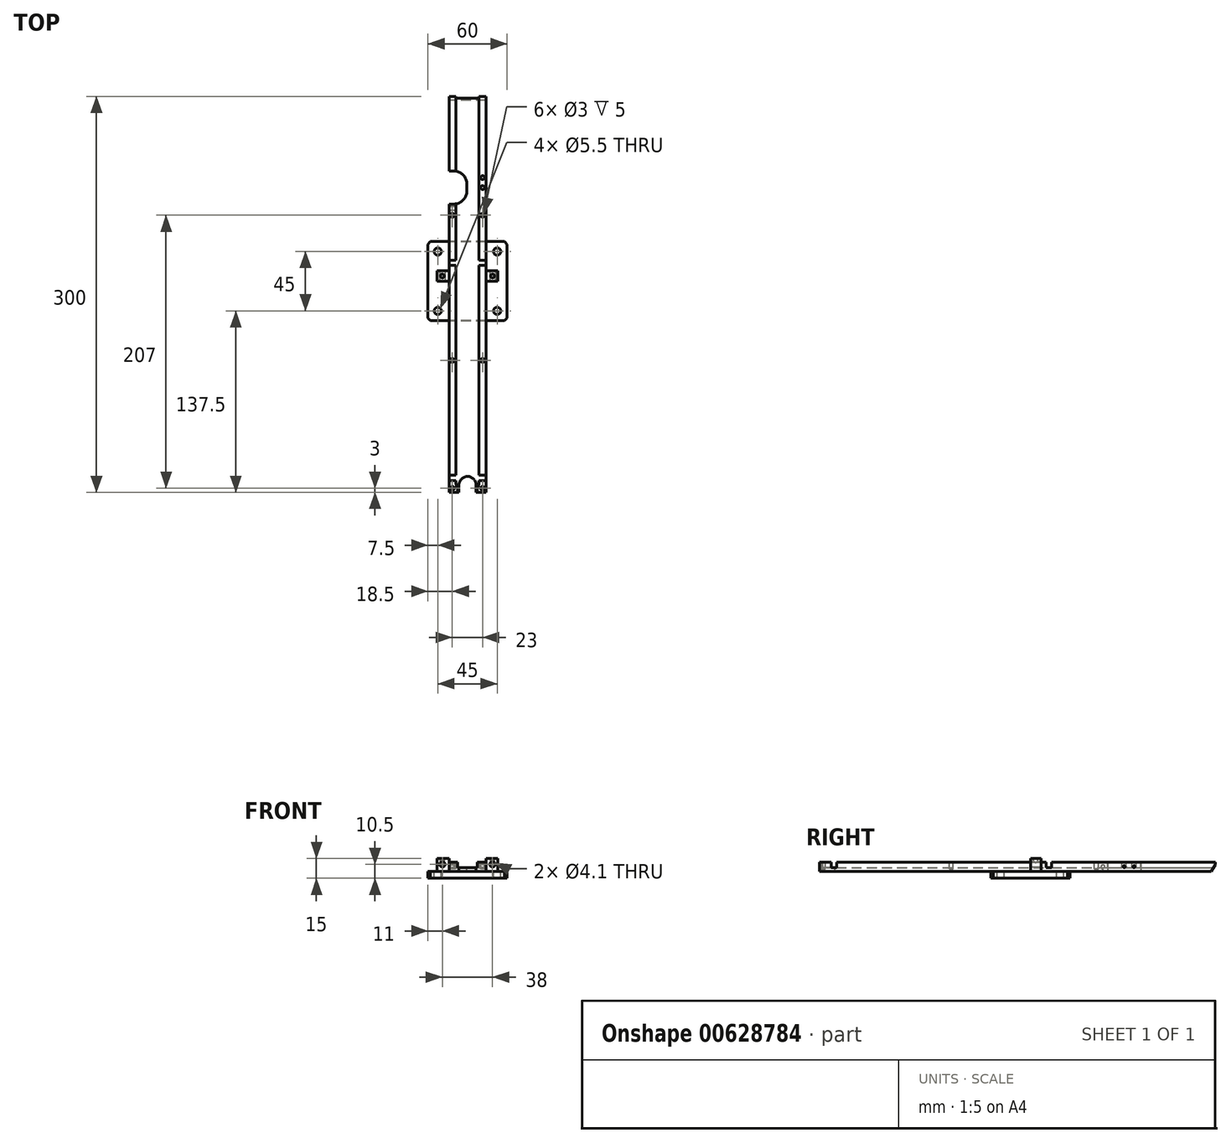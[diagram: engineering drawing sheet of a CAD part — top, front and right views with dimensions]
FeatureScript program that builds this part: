
annotation { "Feature Type Name" : "Feature", "Feature Type Description" : "" }
export const myFeature = defineFeature(function(context is Context, id is Id, definition is map)
    precondition{}
    {
        {
            var Q0;
            Q0=qCreatedBy(makeId("Front.planeOp"),FACE);
            var sketch = newSketch(context, id + "F0", { "sketchPlane" : qUnion([Q0])});
            skLineSegment(sketch, "E0.bottom", {"start": v(-30, 2.5) * mm, "end": v(-14, 2.5) * mm});
            skLineSegment(sketch, "E0.top", {"start": v(-30, -2.5) * mm, "end": v(30, -2.5) * mm});
            skLineSegment(sketch, "E0.left", {"start": v(-30, 2.5) * mm, "end": v(-30, -2.5) * mm});
            skLineSegment(sketch, "E0.right", {"start": v(30, 2.5) * mm, "end": v(30, -2.5) * mm});
            skPoint(sketch, "E0.middle", {"position": v(0, 0) * mm});
            skLineSegment(sketch, "E1.bottom", {"start": v(-14, 9.5) * mm, "end": v(-8.7, 9.5) * mm});
            skLineSegment(sketch, "E1.left", {"start": v(-14, 9.5) * mm, "end": v(-14, 2.5) * mm});
            skLineSegment(sketch, "E1.right", {"start": v(14, 9.5) * mm, "end": v(14, 2.5) * mm});
            skLineSegment(sketch, "E2.0", {"start": v(-8.7, 5.5) * mm, "end": v(8.7, 5.5) * mm});
            skLineSegment(sketch, "E3.left", {"start": v(-8.7, 9.5) * mm, "end": v(-8.7, 5.5) * mm});
            skLineSegment(sketch, "E3.right", {"start": v(8.7, 9.5) * mm, "end": v(8.7, 5.5) * mm});
            skLineSegment(sketch, "E4.trimOffspring", {"start": v(8.7, 9.5) * mm, "end": v(14, 9.5) * mm});
            skLineSegment(sketch, "E5.trimOffspring", {"start": v(14, 2.5) * mm, "end": v(30, 2.5) * mm});
            skSolve(sketch);
        }
        {
            var Q0;
            Q0 = qSketchRegion(id + "F0", true);
            extrude(context, id + "F1", {"entities" : qUnion([Q0]), "depth" : 60 * mm, "offsetDistance" : 25 * mm});
        }
        {
            var Q0;
            Q0=makeQuery(id+"F1.opExtrude","CAP_FACE",FACE,{"disambiguationData":[OSD([sQuery(id+"F0.wireOp",EDGE,"E0.bottom"),sQuery(id+"F0.wireOp",EDGE,"E0.top"),sQuery(id+"F0.wireOp",EDGE,"E0.left"),sQuery(id+"F0.wireOp",EDGE,"E0.right"),sQuery(id+"F0.wireOp",EDGE,"E1.bottom"),sQuery(id+"F0.wireOp",EDGE,"E1.left"),sQuery(id+"F0.wireOp",EDGE,"E1.right"),sQuery(id+"F0.wireOp",EDGE,"E2.0"),sQuery(id+"F0.wireOp",EDGE,"E3.left"),sQuery(id+"F0.wireOp",EDGE,"E3.right"),sQuery(id+"F0.wireOp",EDGE,"E4.trimOffspring"),sQuery(id+"F0.wireOp",EDGE,"E5.trimOffspring")])],"isStart":false});
            var sketch = newSketch(context, id + "F2", { "sketchPlane" : qUnion([Q0])});
            skLineSegment(sketch, "E6.0.0", {"start": v(14, 9.5) * mm, "end": v(8.7, 9.5) * mm});
            skLineSegment(sketch, "E6.0.1", {"start": v(8.7, 9.5) * mm, "end": v(8.7, 5.5) * mm});
            skLineSegment(sketch, "E6.0.2", {"start": v(8.7, 5.5) * mm, "end": v(-8.7, 5.5) * mm});
            skLineSegment(sketch, "E6.0.3", {"start": v(-8.7, 5.5) * mm, "end": v(-8.7, 9.5) * mm});
            skLineSegment(sketch, "E6.0.4", {"start": v(-8.7, 9.5) * mm, "end": v(-14, 9.5) * mm});
            skLineSegment(sketch, "E6.0.5", {"start": v(-14, 9.5) * mm, "end": v(-14, 2.5) * mm});
            skLineSegment(sketch, "E6.0.11", {"start": v(14, 2.5) * mm, "end": v(14, 9.5) * mm});
            skPoint(sketch, "E6.0.7.start.orphan", {"position": v(-30, 2.5) * mm});
            skPoint(sketch, "E6.0.8.start.orphan", {"position": v(-30, -2.5) * mm});
            skPoint(sketch, "E6.0.9.start.orphan", {"position": v(30, -2.5) * mm});
            skPoint(sketch, "E6.0.10.start.orphan", {"position": v(30, 2.5) * mm});
            skLineSegment(sketch, "E7", {"start": v(14, 2.5) * mm, "end": v(-14, 2.5) * mm});
            skSolve(sketch);
        }
        {
            var Q0;
            Q0 = qSketchRegion(id + "F2", true);
            extrude(context, id + "F3", {"entities" : qUnion([Q0]), "operationType" : NewBodyOperationType.ADD, "depth" : 130 * mm, "offsetDistance" : 25 * mm});
        }
        {
            var Q0;
            Q0=makeQuery(id+"F1.opExtrude","CAP_FACE",FACE,{"disambiguationData":[OSD([sQuery(id+"F0.wireOp",EDGE,"E0.bottom"),sQuery(id+"F0.wireOp",EDGE,"E0.top"),sQuery(id+"F0.wireOp",EDGE,"E0.left"),sQuery(id+"F0.wireOp",EDGE,"E0.right"),sQuery(id+"F0.wireOp",EDGE,"E1.bottom"),sQuery(id+"F0.wireOp",EDGE,"E1.left"),sQuery(id+"F0.wireOp",EDGE,"E1.right"),sQuery(id+"F0.wireOp",EDGE,"E2.0"),sQuery(id+"F0.wireOp",EDGE,"E3.left"),sQuery(id+"F0.wireOp",EDGE,"E3.right"),sQuery(id+"F0.wireOp",EDGE,"E4.trimOffspring"),sQuery(id+"F0.wireOp",EDGE,"E5.trimOffspring")])],"isStart":true});
            var sketch = newSketch(context, id + "F4", { "sketchPlane" : qUnion([Q0])});
            skLineSegment(sketch, "E8.0.0", {"start": v(-8.7, 9.5) * mm, "end": v(-14, 9.5) * mm});
            skLineSegment(sketch, "E8.0.1", {"start": v(-14, 9.5) * mm, "end": v(-14, 2.5) * mm});
            skLineSegment(sketch, "E8.0.7", {"start": v(14, 2.5) * mm, "end": v(14, 9.5) * mm});
            skLineSegment(sketch, "E8.0.8", {"start": v(14, 9.5) * mm, "end": v(8.7, 9.5) * mm});
            skLineSegment(sketch, "E8.0.9", {"start": v(8.7, 9.5) * mm, "end": v(8.7, 5.5) * mm});
            skLineSegment(sketch, "E8.0.10", {"start": v(8.7, 5.5) * mm, "end": v(-8.7, 5.5) * mm});
            skLineSegment(sketch, "E8.0.11", {"start": v(-8.7, 5.5) * mm, "end": v(-8.7, 9.5) * mm});
            skLineSegment(sketch, "E9", {"start": v(-14, 2.5) * mm, "end": v(14, 2.5) * mm});
            skPoint(sketch, "E8.0.3.start.orphan", {"position": v(-30, 2.5) * mm});
            skPoint(sketch, "E8.0.4.start.orphan", {"position": v(-30, -2.5) * mm});
            skPoint(sketch, "E8.0.5.start.orphan", {"position": v(30, -2.5) * mm});
            skPoint(sketch, "E8.0.6.start.orphan", {"position": v(30, 2.5) * mm});
            skSolve(sketch);
        }
        {
            var Q0;
            Q0 = qSketchRegion(id + "F4", true);
            extrude(context, id + "F5", {"entities" : qUnion([Q0]), "operationType" : NewBodyOperationType.ADD, "depth" : 110 * mm, "offsetDistance" : 25 * mm});
        }
        {
            var Q0;
            Q0=makeQuery(id+"F1.opExtrude","SWEPT_FACE",FACE,{"disambiguationData":[OSD([sQuery(id+"F0.wireOp",EDGE,"E0.bottom")])]});
            var sketch = newSketch(context, id + "F6", { "sketchPlane" : qUnion([Q0])});
            skCircle(sketch, "E10", {"center": v(-22.5, -7.5) * mm, "radius": 2.75 * mm});
            skCircle(sketch, "E11.MirrorC", {"center": v(22.5, -7.5) * mm, "radius": 2.75 * mm});
            skCircle(sketch, "E12", {"center": v(-22.5, -52.5) * mm, "radius": 2.75 * mm});
            skCircle(sketch, "E13", {"center": v(22.5, -52.5) * mm, "radius": 2.75 * mm});
            skSolve(sketch);
        }
        {
            var Q0;
            Q0 = qSketchRegion(id + "F6", true);
            extrude(context, id + "F7", {"entities" : qUnion([Q0]), "operationType" : NewBodyOperationType.REMOVE, "endBound" : BoundingType.THROUGH_ALL, "oppositeDirection" : true, "depth" : 25 * mm, "offsetDistance" : 25 * mm});
        }
        {
            var Q0;
            Q0=makeQuery(id+"F1.opExtrude","SWEPT_FACE",FACE,{"disambiguationData":[OSD([sQuery(id+"F0.wireOp",EDGE,"E0.bottom")])]});
            var sketch = newSketch(context, id + "F8", { "sketchPlane" : qUnion([Q0])});
            skLineSegment(sketch, "E14.bottom", {"start": v(-14, -22) * mm, "end": v(-23, -22) * mm});
            skLineSegment(sketch, "E14.top", {"start": v(-14, -30) * mm, "end": v(-23, -30) * mm});
            skLineSegment(sketch, "E14.left", {"start": v(-14, -22) * mm, "end": v(-14, -30) * mm});
            skLineSegment(sketch, "E14.right", {"start": v(-23, -22) * mm, "end": v(-23, -30) * mm});
            skLineSegment(sketch, "E15.MirrorCS", {"start": v(14, -22) * mm, "end": v(23, -22) * mm});
            skLineSegment(sketch, "E16.MirrorCS", {"start": v(14, -22) * mm, "end": v(14, -30) * mm});
            skLineSegment(sketch, "E17.MirrorCS", {"start": v(14, -30) * mm, "end": v(23, -30) * mm});
            skLineSegment(sketch, "E18.MirrorCS", {"start": v(23, -22) * mm, "end": v(23, -30) * mm});
            skSolve(sketch);
        }
        {
            var Q0;
            Q0 = qSketchRegion(id + "F8", true);
            extrude(context, id + "F9", {"entities" : qUnion([Q0]), "operationType" : NewBodyOperationType.ADD, "depth" : 10 * mm, "offsetDistance" : 25 * mm});
        }
        {
            var Q0;
            Q0=makeQuery(id+"F9.opExtrude","CAP_FACE",FACE,{"disambiguationData":[OSD([sQuery(id+"F8.wireOp",EDGE,"E14.bottom"),sQuery(id+"F8.wireOp",EDGE,"E14.top"),sQuery(id+"F8.wireOp",EDGE,"E14.left"),sQuery(id+"F8.wireOp",EDGE,"E14.right")])],"isStart":false});
            var sketch = newSketch(context, id + "F10", { "sketchPlane" : qUnion([Q0])});
            skCircle(sketch, "E19", {"center": v(-19, -26) * mm, "radius": 1.5 * mm});
            skCircle(sketch, "E20.MirrorC", {"center": v(19, -26) * mm, "radius": 1.5 * mm});
            skSolve(sketch);
        }
        {
            var Q0;
            Q0 = qSketchRegion(id + "F10", true);
            extrude(context, id + "F11", {"entities" : qUnion([Q0]), "operationType" : NewBodyOperationType.REMOVE, "oppositeDirection" : true, "depth" : 4.5 * mm, "offsetDistance" : 25 * mm});
        }
        {
            var Q0;
            Q0=makeQuery(id+"F9.opExtrude","SWEPT_FACE",FACE,{"disambiguationData":[OSD([sQuery(id+"F8.wireOp",EDGE,"E14.top")])]});
            var sketch = newSketch(context, id + "F12", { "sketchPlane" : qUnion([Q0])});
            skCircle(sketch, "E21", {"center": v(-19, 8) * mm, "radius": 2.05 * mm});
            skCircle(sketch, "E22", {"center": v(19, 8) * mm, "radius": 2.05 * mm});
            skSolve(sketch);
        }
        {
            var Q0;
            Q0 = qSketchRegion(id + "F12", true);
            extrude(context, id + "F13", {"entities" : qUnion([Q0]), "operationType" : NewBodyOperationType.REMOVE, "endBound" : BoundingType.THROUGH_ALL, "oppositeDirection" : true, "depth" : 25 * mm, "offsetDistance" : 25 * mm});
        }
        {
            var Q0;
            Q0=makeQuery(id+"F1.opExtrude","CAP_EDGE",EDGE,{"disambiguationData":[OSD([sQuery(id+"F0.wireOp",EDGE,"E0.left")])],"isStart":false});
            var Q1;
            Q1=makeQuery(id+"F1.opExtrude","CAP_EDGE",EDGE,{"disambiguationData":[OSD([sQuery(id+"F0.wireOp",EDGE,"E0.right")])],"isStart":false});
            var Q2;
            Q2=makeQuery(id+"F1.opExtrude","CAP_EDGE",EDGE,{"disambiguationData":[OSD([sQuery(id+"F0.wireOp",EDGE,"E0.right")])],"isStart":true});
            var Q3;
            Q3=makeQuery(id+"F1.opExtrude","CAP_EDGE",EDGE,{"disambiguationData":[OSD([sQuery(id+"F0.wireOp",EDGE,"E0.left")])],"isStart":true});
            chamfer(context, id + "F14", {"entities" : qUnion([Q0, Q1, Q2, Q3]), "width" : 2 * mm, "tangentPropagation" : true});
        }
        {
            var Q0;
            {var subQ1=sQuery(id+"F0.wireOp",EDGE,"E1.left");var subQ4=sQuery(id+"F4.wireOp",EDGE,"E9");var subQ5=sQuery(id+"F4.wireOp",EDGE,"E8.0.7");Q0=makeQuery(id+"F9.boolean.opBoolean","SPLIT",FACE,{"disambiguationData":[TD([makeQuery(id+"F5.opExtrude","SWEPT_FACE",FACE,{"disambiguationData":[OSD([subQ4])]})])],"derivedFrom":makeQuery(id+"F5.boolean.opBoolean","MERGE",FACE,{"derivedFrom":[makeQuery(id+"F3.boolean.opBoolean","MERGE",FACE,{"derivedFrom":[makeQuery(id+"F1.opExtrude","SWEPT_FACE",FACE,{"disambiguationData":[OSD([subQ1])]}),makeQuery(id+"F3.opExtrude","SWEPT_FACE",FACE,{"disambiguationData":[OSD([sQuery(id+"F2.wireOp",EDGE,"E6.0.5")])]})]}),makeQuery(id+"F5.opExtrude","SWEPT_FACE",FACE,{"disambiguationData":[OSD([subQ5])]})]})});}
            var sketch = newSketch(context, id + "F15", { "sketchPlane" : qUnion([Q0])});
            skLineSegment(sketch, "E23.bottom", {"start": v(14, 9.5) * mm, "end": v(18, 9.5) * mm});
            skLineSegment(sketch, "E23.top", {"start": v(14, 5.5) * mm, "end": v(18, 5.5) * mm});
            skLineSegment(sketch, "E23.left", {"start": v(14, 9.5) * mm, "end": v(14, 5.5) * mm});
            skLineSegment(sketch, "E23.right", {"start": v(18, 9.5) * mm, "end": v(18, 5.5) * mm});
            skLineSegment(sketch, "E24.bottom", {"start": v(177, 9.5) * mm, "end": v(181, 9.5) * mm});
            skLineSegment(sketch, "E24.top", {"start": v(177, 5.5) * mm, "end": v(181, 5.5) * mm});
            skLineSegment(sketch, "E24.left", {"start": v(177, 9.5) * mm, "end": v(177, 5.5) * mm});
            skLineSegment(sketch, "E24.right", {"start": v(181, 9.5) * mm, "end": v(181, 5.5) * mm});
            skSolve(sketch);
        }
        {
            var Q0;
            Q0 = qSketchRegion(id + "F15", true);
            extrude(context, id + "F16", {"entities" : qUnion([Q0]), "operationType" : NewBodyOperationType.REMOVE, "endBound" : BoundingType.THROUGH_ALL, "oppositeDirection" : true, "depth" : 25 * mm, "offsetDistance" : 25 * mm});
        }
        {
            var Q0;
            {var subQ1=sQuery(id+"F0.wireOp",EDGE,"E1.left");var subQ4=sQuery(id+"F4.wireOp",EDGE,"E9");var subQ5=sQuery(id+"F4.wireOp",EDGE,"E8.0.7");Q0=makeQuery(id+"F9.boolean.opBoolean","SPLIT",FACE,{"disambiguationData":[TD([makeQuery(id+"F5.opExtrude","SWEPT_FACE",FACE,{"disambiguationData":[OSD([subQ4])]})])],"derivedFrom":makeQuery(id+"F5.boolean.opBoolean","MERGE",FACE,{"derivedFrom":[makeQuery(id+"F3.boolean.opBoolean","MERGE",FACE,{"derivedFrom":[makeQuery(id+"F1.opExtrude","SWEPT_FACE",FACE,{"disambiguationData":[OSD([subQ1])]}),makeQuery(id+"F3.opExtrude","SWEPT_FACE",FACE,{"disambiguationData":[OSD([sQuery(id+"F2.wireOp",EDGE,"E6.0.5")])]})]}),makeQuery(id+"F5.opExtrude","SWEPT_FACE",FACE,{"disambiguationData":[OSD([subQ5])]})]})});}
            var sketch = newSketch(context, id + "F17", { "sketchPlane" : qUnion([Q0])});
            skLineSegment(sketch, "E25", {"start": v(-110, 7.7) * mm, "end": v(-107, 2.5) * mm});
            skLineSegment(sketch, "E26", {"start": v(-107, 2.5) * mm, "end": v(-110, 2.5) * mm});
            skLineSegment(sketch, "E27", {"start": v(-110, 2.5) * mm, "end": v(-110, 7.7) * mm});
            skSolve(sketch);
        }
        {
            var Q0;
            Q0 = qSketchRegion(id + "F17", true);
            extrude(context, id + "F18", {"entities" : qUnion([Q0]), "operationType" : NewBodyOperationType.REMOVE, "endBound" : BoundingType.THROUGH_ALL, "oppositeDirection" : true, "depth" : 25 * mm, "offsetDistance" : 25 * mm});
        }
        {
            var Q0;
            Q0=makeQuery(id+"F16.boolean.opBoolean","MERGE",FACE,{"derivedFrom":[makeQuery(id+"F5.boolean.opBoolean","MERGE",FACE,{"derivedFrom":[makeQuery(id+"F3.boolean.opBoolean","MERGE",FACE,{"derivedFrom":[makeQuery(id+"F1.opExtrude","SWEPT_FACE",FACE,{"disambiguationData":[OSD([sQuery(id+"F0.wireOp",EDGE,"E2.0")])]}),makeQuery(id+"F3.opExtrude","SWEPT_FACE",FACE,{"disambiguationData":[OSD([sQuery(id+"F2.wireOp",EDGE,"E6.0.2")])]})]}),makeQuery(id+"F5.opExtrude","SWEPT_FACE",FACE,{"disambiguationData":[OSD([sQuery(id+"F4.wireOp",EDGE,"E8.0.10")])]})]}),makeQuery(id+"F16.opExtrude","SWEPT_FACE",FACE,{"disambiguationData":[OSD([sQuery(id+"F15.wireOp",EDGE,"E23.top")])]}),makeQuery(id+"F16.opExtrude","SWEPT_FACE",FACE,{"disambiguationData":[OSD([sQuery(id+"F15.wireOp",EDGE,"E24.top")])]})]});
            var sketch = newSketch(context, id + "F19", { "sketchPlane" : qUnion([Q0])});
            skLineSegment(sketch, "E28.bottom", {"start": v(8.7, -190) * mm, "end": v(-8.7, -190) * mm});
            skLineSegment(sketch, "E28.top", {"start": v(8.7, -175) * mm, "end": v(-8.7, -175) * mm});
            skLineSegment(sketch, "E28.left", {"start": v(8.7, -190) * mm, "end": v(8.7, -175) * mm});
            skLineSegment(sketch, "E28.right", {"start": v(-8.7, -190) * mm, "end": v(-8.7, -175) * mm});
            skSolve(sketch);
        }
        {
            var Q0;
            Q0 = qSketchRegion(id + "F19", true);
            var Q1;
            {var subQ2=sQuery(id+"F2.wireOp",EDGE,"E6.0.4");Q1=makeQuery(id+"F16.boolean.opBoolean","SPLIT",FACE,{"disambiguationData":[TD([makeQuery(id+"F16.opExtrude","SWEPT_FACE",FACE,{"disambiguationData":[OSD([sQuery(id+"F15.wireOp",EDGE,"E24.right")])]})])],"derivedFrom":makeQuery(id+"F5.boolean.opBoolean","MERGE",FACE,{"derivedFrom":[makeQuery(id+"F3.boolean.opBoolean","MERGE",FACE,{"derivedFrom":[makeQuery(id+"F1.opExtrude","SWEPT_FACE",FACE,{"disambiguationData":[OSD([sQuery(id+"F0.wireOp",EDGE,"E1.bottom")])]}),makeQuery(id+"F3.opExtrude","SWEPT_FACE",FACE,{"disambiguationData":[OSD([subQ2])]})]}),makeQuery(id+"F5.opExtrude","SWEPT_FACE",FACE,{"disambiguationData":[OSD([sQuery(id+"F4.wireOp",EDGE,"E8.0.8")])]})]})});}
            extrude(context, id + "F20", {"entities" : qUnion([Q0]), "operationType" : NewBodyOperationType.ADD, "endBound" : BoundingType.UP_TO_SURFACE, "depth" : 25 * mm, "endBoundEntityFace" : qUnion([Q1]), "offsetDistance" : 25 * mm});
        }
        {
            var Q0;
            {var subQ10=sQuery(id+"F2.wireOp",EDGE,"E6.0.0");var subQ11=makeQuery(id+"F5.boolean.opBoolean","MERGE",FACE,{"derivedFrom":[makeQuery(id+"F3.boolean.opBoolean","MERGE",FACE,{"derivedFrom":[makeQuery(id+"F1.opExtrude","SWEPT_FACE",FACE,{"disambiguationData":[OSD([sQuery(id+"F0.wireOp",EDGE,"E4.trimOffspring")])]}),makeQuery(id+"F3.opExtrude","SWEPT_FACE",FACE,{"disambiguationData":[OSD([subQ10])]})]}),makeQuery(id+"F5.opExtrude","SWEPT_FACE",FACE,{"disambiguationData":[OSD([sQuery(id+"F4.wireOp",EDGE,"E8.0.0")])]})]});var subQ13=sQuery(id+"F2.wireOp",EDGE,"E6.0.4");var subQ16=makeQuery(id+"F16.opExtrude","SWEPT_FACE",FACE,{"disambiguationData":[OSD([sQuery(id+"F15.wireOp",EDGE,"E24.right")])]});var subQ23=makeQuery(id+"F5.boolean.opBoolean","MERGE",FACE,{"derivedFrom":[makeQuery(id+"F3.boolean.opBoolean","MERGE",FACE,{"derivedFrom":[makeQuery(id+"F1.opExtrude","SWEPT_FACE",FACE,{"disambiguationData":[OSD([sQuery(id+"F0.wireOp",EDGE,"E1.bottom")])]}),makeQuery(id+"F3.opExtrude","SWEPT_FACE",FACE,{"disambiguationData":[OSD([subQ13])]})]}),makeQuery(id+"F5.opExtrude","SWEPT_FACE",FACE,{"disambiguationData":[OSD([sQuery(id+"F4.wireOp",EDGE,"E8.0.8")])]})]});Q0=makeQuery(id+"F20.boolean.opBoolean","MERGE",FACE,{"derivedFrom":[makeQuery(id+"F16.boolean.opBoolean","SPLIT",FACE,{"disambiguationData":[TD([subQ16])],"derivedFrom":subQ23}),makeQuery(id+"F16.boolean.opBoolean","SPLIT",FACE,{"disambiguationData":[TD([makeQuery(id+"F9.opExtrude","SWEPT_FACE",FACE,{"disambiguationData":[OSD([sQuery(id+"F8.wireOp",EDGE,"E14.bottom")])]})])],"derivedFrom":subQ23}),makeQuery(id+"F16.boolean.opBoolean","SPLIT",FACE,{"disambiguationData":[TD([subQ16])],"derivedFrom":subQ11}),makeQuery(id+"F16.boolean.opBoolean","SPLIT",FACE,{"disambiguationData":[TD([makeQuery(id+"F9.opExtrude","SWEPT_FACE",FACE,{"disambiguationData":[OSD([sQuery(id+"F8.wireOp",EDGE,"E15.MirrorCS")])]})])],"derivedFrom":subQ11}),makeQuery(id+"F20.opExtrude","CAP_FACE",FACE,{"disambiguationData":[OSD([sQuery(id+"F19.wireOp",EDGE,"E28.bottom"),sQuery(id+"F19.wireOp",EDGE,"E28.top"),sQuery(id+"F19.wireOp",EDGE,"E28.left"),sQuery(id+"F19.wireOp",EDGE,"E28.right")])],"isStart":false})]});}
            var sketch = newSketch(context, id + "F21", { "sketchPlane" : qUnion([Q0])});
            skLineSegment(sketch, "E29.bottom", {"start": v(6.5, -190) * mm, "end": v(-6.5, -190) * mm});
            skLineSegment(sketch, "E29.left", {"start": v(6.5, -190) * mm, "end": v(6.5, -184.5) * mm});
            skLineSegment(sketch, "E29.right", {"start": v(-6.5, -190) * mm, "end": v(-6.5, -184.5) * mm});
            skPoint(sketch, "E30.endSnap0", {"position": v(0, -190) * mm});
            skArc(sketch, "E31", {"start": v(6.5, -184.5) * mm, "mid": v(0, -178) * mm, "end": v(-6.5, -184.5) * mm});
            skPoint(sketch, "E32.orphan", {"position": v(0, -183) * mm});
            skPoint(sketch, "E30.start.orphan", {"position": v(0, -190) * mm});
            skSolve(sketch);
        }
        {
            var Q0;
            Q0 = qSketchRegion(id + "F21", true);
            extrude(context, id + "F22", {"entities" : qUnion([Q0]), "operationType" : NewBodyOperationType.REMOVE, "endBound" : BoundingType.THROUGH_ALL, "oppositeDirection" : true, "depth" : 25 * mm, "offsetDistance" : 25 * mm});
        }
        {
            var Q0;
            {var subQ10=sQuery(id+"F2.wireOp",EDGE,"E6.0.0");var subQ11=makeQuery(id+"F5.boolean.opBoolean","MERGE",FACE,{"derivedFrom":[makeQuery(id+"F3.boolean.opBoolean","MERGE",FACE,{"derivedFrom":[makeQuery(id+"F1.opExtrude","SWEPT_FACE",FACE,{"disambiguationData":[OSD([sQuery(id+"F0.wireOp",EDGE,"E4.trimOffspring")])]}),makeQuery(id+"F3.opExtrude","SWEPT_FACE",FACE,{"disambiguationData":[OSD([subQ10])]})]}),makeQuery(id+"F5.opExtrude","SWEPT_FACE",FACE,{"disambiguationData":[OSD([sQuery(id+"F4.wireOp",EDGE,"E8.0.0")])]})]});var subQ13=sQuery(id+"F2.wireOp",EDGE,"E6.0.4");var subQ16=makeQuery(id+"F16.opExtrude","SWEPT_FACE",FACE,{"disambiguationData":[OSD([sQuery(id+"F15.wireOp",EDGE,"E24.right")])]});var subQ23=makeQuery(id+"F5.boolean.opBoolean","MERGE",FACE,{"derivedFrom":[makeQuery(id+"F3.boolean.opBoolean","MERGE",FACE,{"derivedFrom":[makeQuery(id+"F1.opExtrude","SWEPT_FACE",FACE,{"disambiguationData":[OSD([sQuery(id+"F0.wireOp",EDGE,"E1.bottom")])]}),makeQuery(id+"F3.opExtrude","SWEPT_FACE",FACE,{"disambiguationData":[OSD([subQ13])]})]}),makeQuery(id+"F5.opExtrude","SWEPT_FACE",FACE,{"disambiguationData":[OSD([sQuery(id+"F4.wireOp",EDGE,"E8.0.8")])]})]});Q0=makeQuery(id+"F20.boolean.opBoolean","MERGE",FACE,{"derivedFrom":[makeQuery(id+"F16.boolean.opBoolean","SPLIT",FACE,{"disambiguationData":[TD([subQ16])],"derivedFrom":subQ23}),makeQuery(id+"F16.boolean.opBoolean","SPLIT",FACE,{"disambiguationData":[TD([makeQuery(id+"F9.opExtrude","SWEPT_FACE",FACE,{"disambiguationData":[OSD([sQuery(id+"F8.wireOp",EDGE,"E14.bottom")])]})])],"derivedFrom":subQ23}),makeQuery(id+"F16.boolean.opBoolean","SPLIT",FACE,{"disambiguationData":[TD([subQ16])],"derivedFrom":subQ11}),makeQuery(id+"F16.boolean.opBoolean","SPLIT",FACE,{"disambiguationData":[TD([makeQuery(id+"F9.opExtrude","SWEPT_FACE",FACE,{"disambiguationData":[OSD([sQuery(id+"F8.wireOp",EDGE,"E15.MirrorCS")])]})])],"derivedFrom":subQ11}),makeQuery(id+"F20.opExtrude","CAP_FACE",FACE,{"disambiguationData":[OSD([sQuery(id+"F19.wireOp",EDGE,"E28.bottom"),sQuery(id+"F19.wireOp",EDGE,"E28.top"),sQuery(id+"F19.wireOp",EDGE,"E28.left"),sQuery(id+"F19.wireOp",EDGE,"E28.right")])],"isStart":false})]});}
            var sketch = newSketch(context, id + "F23", { "sketchPlane" : qUnion([Q0])});
            skCircle(sketch, "E33", {"center": v(0, -183) * mm, "radius": 8.7 * mm});
            skPoint(sketch, "E33.centerSnap0", {"position": v(0, -175) * mm});
            skSolve(sketch);
        }
        {
            var Q0;
            Q0 = qSketchRegion(id + "F23", true);
            var Q1;
            {var subQ9=makeQuery(id+"F1.opExtrude","SWEPT_FACE",FACE,{"disambiguationData":[OSD([sQuery(id+"F0.wireOp",EDGE,"E3.left")])]});var subQ13=makeQuery(id+"F3.opExtrude","SWEPT_FACE",FACE,{"disambiguationData":[OSD([sQuery(id+"F2.wireOp",EDGE,"E6.0.2")])]});var subQ14=makeQuery(id+"F16.opExtrude","SWEPT_FACE",FACE,{"disambiguationData":[OSD([sQuery(id+"F15.wireOp",EDGE,"E24.top")])]});var subQ15=makeQuery(id+"F1.opExtrude","SWEPT_FACE",FACE,{"disambiguationData":[OSD([sQuery(id+"F0.wireOp",EDGE,"E2.0")])]});var subQ18=makeQuery(id+"F5.opExtrude","SWEPT_FACE",FACE,{"disambiguationData":[OSD([sQuery(id+"F4.wireOp",EDGE,"E8.0.10")])]});var subQ19=makeQuery(id+"F16.opExtrude","SWEPT_FACE",FACE,{"disambiguationData":[OSD([sQuery(id+"F15.wireOp",EDGE,"E23.top")])]});Q1=makeQuery(id+"F20.boolean.opBoolean","SPLIT",FACE,{"disambiguationData":[TD([subQ9])],"derivedFrom":makeQuery(id+"F16.boolean.opBoolean","MERGE",FACE,{"derivedFrom":[makeQuery(id+"F5.boolean.opBoolean","MERGE",FACE,{"derivedFrom":[makeQuery(id+"F3.boolean.opBoolean","MERGE",FACE,{"derivedFrom":[subQ15,subQ13]}),subQ18]}),subQ19,subQ14]})});}
            extrude(context, id + "F24", {"entities" : qUnion([Q0]), "operationType" : NewBodyOperationType.REMOVE, "endBound" : BoundingType.UP_TO_SURFACE, "oppositeDirection" : true, "depth" : 25 * mm, "endBoundEntityFace" : qUnion([Q1]), "offsetDistance" : 25 * mm});
        }
        {
            var Q0;
            {var subQ9=makeQuery(id+"F1.opExtrude","SWEPT_FACE",FACE,{"disambiguationData":[OSD([sQuery(id+"F0.wireOp",EDGE,"E3.left")])]});var subQ13=makeQuery(id+"F3.opExtrude","SWEPT_FACE",FACE,{"disambiguationData":[OSD([sQuery(id+"F2.wireOp",EDGE,"E6.0.2")])]});var subQ14=makeQuery(id+"F16.opExtrude","SWEPT_FACE",FACE,{"disambiguationData":[OSD([sQuery(id+"F15.wireOp",EDGE,"E24.top")])]});var subQ15=makeQuery(id+"F1.opExtrude","SWEPT_FACE",FACE,{"disambiguationData":[OSD([sQuery(id+"F0.wireOp",EDGE,"E2.0")])]});var subQ18=makeQuery(id+"F5.opExtrude","SWEPT_FACE",FACE,{"disambiguationData":[OSD([sQuery(id+"F4.wireOp",EDGE,"E8.0.10")])]});var subQ19=makeQuery(id+"F16.opExtrude","SWEPT_FACE",FACE,{"disambiguationData":[OSD([sQuery(id+"F15.wireOp",EDGE,"E23.top")])]});Q0=makeQuery(id+"F24.boolean.opBoolean","MERGE",FACE,{"derivedFrom":[makeQuery(id+"F20.boolean.opBoolean","SPLIT",FACE,{"disambiguationData":[TD([subQ9])],"derivedFrom":makeQuery(id+"F16.boolean.opBoolean","MERGE",FACE,{"derivedFrom":[makeQuery(id+"F5.boolean.opBoolean","MERGE",FACE,{"derivedFrom":[makeQuery(id+"F3.boolean.opBoolean","MERGE",FACE,{"derivedFrom":[subQ15,subQ13]}),subQ18]}),subQ19,subQ14]})}),makeQuery(id+"F24.opExtrude","CAP_FACE",FACE,{"disambiguationData":[OSD([sQuery(id+"F23.wireOp",EDGE,"E33")])],"isStart":false})]});}
            var sketch = newSketch(context, id + "F25", { "sketchPlane" : qUnion([Q0])});
            skLineSegment(sketch, "E34.bottom", {"start": v(8.7, -175) * mm, "end": v(-8.7, -175) * mm});
            skLineSegment(sketch, "E34.top", {"start": v(8.7, -183) * mm, "end": v(-8.7, -183) * mm});
            skLineSegment(sketch, "E34.left", {"start": v(8.7, -175) * mm, "end": v(8.7, -183) * mm});
            skLineSegment(sketch, "E34.right", {"start": v(-8.7, -175) * mm, "end": v(-8.7, -183) * mm});
            skSolve(sketch);
        }
        {
            var Q0;
            Q0 = qSketchRegion(id + "F25", true);
            var Q1;
            {var subQ1=makeQuery(id+"F1.opExtrude","SWEPT_FACE",FACE,{"disambiguationData":[OSD([sQuery(id+"F0.wireOp",EDGE,"E1.right")])]});var subQ5=makeQuery(id+"F9.opExtrude","SWEPT_FACE",FACE,{"disambiguationData":[OSD([sQuery(id+"F8.wireOp",EDGE,"E15.MirrorCS")])]});var subQ9=makeQuery(id+"F5.opExtrude","SWEPT_FACE",FACE,{"disambiguationData":[OSD([sQuery(id+"F4.wireOp",EDGE,"E8.0.0")])]});var subQ13=makeQuery(id+"F1.opExtrude","SWEPT_FACE",FACE,{"disambiguationData":[OSD([sQuery(id+"F0.wireOp",EDGE,"E4.trimOffspring")])]});var subQ15=sQuery(id+"F2.wireOp",EDGE,"E6.0.0");var subQ16=makeQuery(id+"F3.opExtrude","SWEPT_FACE",FACE,{"disambiguationData":[OSD([subQ15])]});var subQ23=sQuery(id+"F2.wireOp",EDGE,"E6.0.4");var subQ26=sQuery(id+"F19.wireOp",EDGE,"E28.left");var subQ27=sQuery(id+"F19.wireOp",EDGE,"E28.bottom");var subQ29=sQuery(id+"F19.wireOp",EDGE,"E28.top");var subQ30=makeQuery(id+"F16.opExtrude","SWEPT_FACE",FACE,{"disambiguationData":[OSD([sQuery(id+"F15.wireOp",EDGE,"E24.right")])]});var subQ31=makeQuery(id+"F5.boolean.opBoolean","MERGE",FACE,{"derivedFrom":[makeQuery(id+"F3.boolean.opBoolean","MERGE",FACE,{"derivedFrom":[subQ13,subQ16]}),subQ9]});var subQ38=makeQuery(id+"F5.boolean.opBoolean","MERGE",FACE,{"derivedFrom":[makeQuery(id+"F3.boolean.opBoolean","MERGE",FACE,{"derivedFrom":[makeQuery(id+"F1.opExtrude","SWEPT_FACE",FACE,{"disambiguationData":[OSD([sQuery(id+"F0.wireOp",EDGE,"E1.bottom")])]}),makeQuery(id+"F3.opExtrude","SWEPT_FACE",FACE,{"disambiguationData":[OSD([subQ23])]})]}),makeQuery(id+"F5.opExtrude","SWEPT_FACE",FACE,{"disambiguationData":[OSD([sQuery(id+"F4.wireOp",EDGE,"E8.0.8")])]})]});Q1=makeQuery(id+"F24.boolean.opBoolean","SPLIT",FACE,{"disambiguationData":[TD([subQ1])],"derivedFrom":makeQuery(id+"F20.boolean.opBoolean","MERGE",FACE,{"derivedFrom":[makeQuery(id+"F16.boolean.opBoolean","SPLIT",FACE,{"disambiguationData":[TD([subQ30])],"derivedFrom":subQ38}),makeQuery(id+"F16.boolean.opBoolean","SPLIT",FACE,{"disambiguationData":[TD([makeQuery(id+"F9.opExtrude","SWEPT_FACE",FACE,{"disambiguationData":[OSD([sQuery(id+"F8.wireOp",EDGE,"E14.bottom")])]})])],"derivedFrom":subQ38}),makeQuery(id+"F16.boolean.opBoolean","SPLIT",FACE,{"disambiguationData":[TD([subQ30])],"derivedFrom":subQ31}),makeQuery(id+"F16.boolean.opBoolean","SPLIT",FACE,{"disambiguationData":[TD([subQ5])],"derivedFrom":subQ31}),makeQuery(id+"F20.opExtrude","CAP_FACE",FACE,{"disambiguationData":[OSD([subQ27,subQ29,subQ26,sQuery(id+"F19.wireOp",EDGE,"E28.right")])],"isStart":false})]})});}
            extrude(context, id + "F26", {"entities" : qUnion([Q0]), "operationType" : NewBodyOperationType.REMOVE, "endBound" : BoundingType.UP_TO_SURFACE, "depth" : 25 * mm, "endBoundEntityFace" : qUnion([Q1]), "offsetDistance" : 25 * mm});
        }
        {
            var Q0;
            Q0=qCreatedBy(makeId("Right.planeOp"),FACE);
            var sketch = newSketch(context, id + "F27", { "sketchPlane" : qUnion([Q0])});
            skLineSegment(sketch, "E35.bottom", {"start": v(32, 6.5) * mm, "end": v(50, 6.5) * mm});
            skLineSegment(sketch, "E35.top", {"start": v(32, 5.5) * mm, "end": v(50, 5.5) * mm});
            skLineSegment(sketch, "E35.left", {"start": v(32, 6.5) * mm, "end": v(32, 5.5) * mm});
            skLineSegment(sketch, "E35.right", {"start": v(50, 6.5) * mm, "end": v(50, 5.5) * mm});
            skSolve(sketch);
        }
        {
            var Q0;
            Q0 = qSketchRegion(id + "F27", true);
            extrude(context, id + "F28", {"entities" : qUnion([Q0]), "operationType" : NewBodyOperationType.REMOVE, "endBound" : BoundingType.THROUGH_ALL, "depth" : 10 * mm, "offsetDistance" : 25 * mm});
        }
        {
            var Q0;
            {var subQ9=makeQuery(id+"F1.opExtrude","SWEPT_FACE",FACE,{"disambiguationData":[OSD([sQuery(id+"F0.wireOp",EDGE,"E3.left")])]});var subQ13=makeQuery(id+"F3.opExtrude","SWEPT_FACE",FACE,{"disambiguationData":[OSD([sQuery(id+"F2.wireOp",EDGE,"E6.0.2")])]});var subQ14=makeQuery(id+"F16.opExtrude","SWEPT_FACE",FACE,{"disambiguationData":[OSD([sQuery(id+"F15.wireOp",EDGE,"E24.top")])]});var subQ15=makeQuery(id+"F1.opExtrude","SWEPT_FACE",FACE,{"disambiguationData":[OSD([sQuery(id+"F0.wireOp",EDGE,"E2.0")])]});var subQ18=makeQuery(id+"F5.opExtrude","SWEPT_FACE",FACE,{"disambiguationData":[OSD([sQuery(id+"F4.wireOp",EDGE,"E8.0.10")])]});var subQ19=makeQuery(id+"F16.opExtrude","SWEPT_FACE",FACE,{"disambiguationData":[OSD([sQuery(id+"F15.wireOp",EDGE,"E23.top")])]});var subQ25=makeQuery(id+"F16.boolean.opBoolean","MERGE",FACE,{"derivedFrom":[makeQuery(id+"F5.boolean.opBoolean","MERGE",FACE,{"derivedFrom":[makeQuery(id+"F3.boolean.opBoolean","MERGE",FACE,{"derivedFrom":[subQ15,subQ13]}),subQ18]}),subQ19,subQ14]});Q0=makeQuery(id+"F28.boolean.opBoolean","MERGE",FACE,{"derivedFrom":[makeQuery(id+"F26.boolean.opBoolean","MERGE",FACE,{"derivedFrom":[makeQuery(id+"F20.boolean.opBoolean","SPLIT",FACE,{"disambiguationData":[TD([makeQuery(id+"F20.opExtrude","SWEPT_FACE",FACE,{"disambiguationData":[OSD([sQuery(id+"F19.wireOp",EDGE,"E28.right")])]})])],"derivedFrom":subQ25}),makeQuery(id+"F20.boolean.opBoolean","SPLIT",FACE,{"disambiguationData":[TD([makeQuery(id+"F20.opExtrude","SWEPT_FACE",FACE,{"disambiguationData":[OSD([sQuery(id+"F19.wireOp",EDGE,"E28.left")])]})])],"derivedFrom":subQ25}),makeQuery(id+"F24.boolean.opBoolean","MERGE",FACE,{"derivedFrom":[makeQuery(id+"F20.boolean.opBoolean","SPLIT",FACE,{"disambiguationData":[TD([subQ9])],"derivedFrom":subQ25}),makeQuery(id+"F24.opExtrude","CAP_FACE",FACE,{"disambiguationData":[OSD([sQuery(id+"F23.wireOp",EDGE,"E33")])],"isStart":false})]}),makeQuery(id+"F26.opExtrude","CAP_FACE",FACE,{"disambiguationData":[OSD([sQuery(id+"F25.wireOp",EDGE,"E34.bottom"),sQuery(id+"F25.wireOp",EDGE,"E34.top"),sQuery(id+"F25.wireOp",EDGE,"E34.left"),sQuery(id+"F25.wireOp",EDGE,"E34.right")])],"isStart":true})]}),makeQuery(id+"F28.opExtrude","SWEPT_FACE",FACE,{"disambiguationData":[OSD([sQuery(id+"F27.wireOp",EDGE,"E35.top")])]})]});}
            var sketch = newSketch(context, id + "F29", { "sketchPlane" : qUnion([Q0])});
            skLineSegment(sketch, "E36.right", {"start": v(-14.2, 53.5) * mm, "end": v(-14.2, 34.9) * mm});
            skPoint(sketch, "E37.centerSnap0", {"position": v(-0.4, 41) * mm});
            skLineSegment(sketch, "E38", {"start": v(-14.2, 34.9) * mm, "end": v(-14.2, 53.5) * mm});
            skPoint(sketch, "E36.left.start.orphan", {"position": v(-0.4, 50) * mm});
            skPoint(sketch, "E39.trimOffspring.end.orphan", {"position": v(-0.4, 32) * mm});
            skLineSegment(sketch, "E40.bottom", {"start": v(-14.2, 53.5) * mm, "end": v(-0.4, 53.5) * mm});
            skLineSegment(sketch, "E40.top", {"start": v(-14.2, 28.5) * mm, "end": v(-0.4, 28.5) * mm});
            skLineSegment(sketch, "E40.left", {"start": v(-14.2, 53.5) * mm, "end": v(-14.2, 28.5) * mm});
            skLineSegment(sketch, "E40.right", {"start": v(-0.4, 53.5) * mm, "end": v(-0.4, 28.5) * mm});
            skSolve(sketch);
        }
        {
            var Q0;
            Q0 = qSketchRegion(id + "F29", true);
            extrude(context, id + "F30", {"entities" : qUnion([Q0]), "operationType" : NewBodyOperationType.REMOVE, "endBound" : BoundingType.SYMMETRIC, "oppositeDirection" : true, "depth" : 30 * mm, "offsetDistance" : 25 * mm});
        }
        {
            var Q0;
            Q0=makeQuery(id+"F30.boolean.opBoolean","COPY",EDGE,{"derivedFrom":makeQuery(id+"F30.opExtrude","SWEPT_EDGE",EDGE,{"disambiguationData":[OSD([sQuery(id+"F29.wireOp",EDGE,"E40.bottom"),sQuery(id+"F29.wireOp",EDGE,"E40.right")])]})});
            var Q1;
            Q1=makeQuery(id+"F30.boolean.opBoolean","COPY",EDGE,{"derivedFrom":makeQuery(id+"F30.opExtrude","SWEPT_EDGE",EDGE,{"disambiguationData":[OSD([sQuery(id+"F29.wireOp",EDGE,"E40.top"),sQuery(id+"F29.wireOp",EDGE,"E40.right")])]})});
            fillet(context, id + "F31", {"entities" : qUnion([Q0, Q1]), "radius" : 10 * mm, "tangentPropagation" : true, "allowEdgeOverflow" : false});
        }
        {
            var Q0;
            {var subQ9=makeQuery(id+"F1.opExtrude","SWEPT_FACE",FACE,{"disambiguationData":[OSD([sQuery(id+"F0.wireOp",EDGE,"E3.left")])]});var subQ13=makeQuery(id+"F3.opExtrude","SWEPT_FACE",FACE,{"disambiguationData":[OSD([sQuery(id+"F2.wireOp",EDGE,"E6.0.2")])]});var subQ14=makeQuery(id+"F16.opExtrude","SWEPT_FACE",FACE,{"disambiguationData":[OSD([sQuery(id+"F15.wireOp",EDGE,"E24.top")])]});var subQ15=makeQuery(id+"F1.opExtrude","SWEPT_FACE",FACE,{"disambiguationData":[OSD([sQuery(id+"F0.wireOp",EDGE,"E2.0")])]});var subQ18=makeQuery(id+"F5.opExtrude","SWEPT_FACE",FACE,{"disambiguationData":[OSD([sQuery(id+"F4.wireOp",EDGE,"E8.0.10")])]});var subQ19=makeQuery(id+"F16.opExtrude","SWEPT_FACE",FACE,{"disambiguationData":[OSD([sQuery(id+"F15.wireOp",EDGE,"E23.top")])]});var subQ25=makeQuery(id+"F16.boolean.opBoolean","MERGE",FACE,{"derivedFrom":[makeQuery(id+"F5.boolean.opBoolean","MERGE",FACE,{"derivedFrom":[makeQuery(id+"F3.boolean.opBoolean","MERGE",FACE,{"derivedFrom":[subQ15,subQ13]}),subQ18]}),subQ19,subQ14]});Q0=makeQuery(id+"F28.boolean.opBoolean","MERGE",FACE,{"derivedFrom":[makeQuery(id+"F26.boolean.opBoolean","MERGE",FACE,{"derivedFrom":[makeQuery(id+"F20.boolean.opBoolean","SPLIT",FACE,{"disambiguationData":[TD([makeQuery(id+"F20.opExtrude","SWEPT_FACE",FACE,{"disambiguationData":[OSD([sQuery(id+"F19.wireOp",EDGE,"E28.right")])]})])],"derivedFrom":subQ25}),makeQuery(id+"F20.boolean.opBoolean","SPLIT",FACE,{"disambiguationData":[TD([makeQuery(id+"F20.opExtrude","SWEPT_FACE",FACE,{"disambiguationData":[OSD([sQuery(id+"F19.wireOp",EDGE,"E28.left")])]})])],"derivedFrom":subQ25}),makeQuery(id+"F24.boolean.opBoolean","MERGE",FACE,{"derivedFrom":[makeQuery(id+"F20.boolean.opBoolean","SPLIT",FACE,{"disambiguationData":[TD([subQ9])],"derivedFrom":subQ25}),makeQuery(id+"F24.opExtrude","CAP_FACE",FACE,{"disambiguationData":[OSD([sQuery(id+"F23.wireOp",EDGE,"E33")])],"isStart":false})]}),makeQuery(id+"F26.opExtrude","CAP_FACE",FACE,{"disambiguationData":[OSD([sQuery(id+"F25.wireOp",EDGE,"E34.bottom"),sQuery(id+"F25.wireOp",EDGE,"E34.top"),sQuery(id+"F25.wireOp",EDGE,"E34.left"),sQuery(id+"F25.wireOp",EDGE,"E34.right")])],"isStart":true})]}),makeQuery(id+"F28.opExtrude","SWEPT_FACE",FACE,{"disambiguationData":[OSD([sQuery(id+"F27.wireOp",EDGE,"E35.top")])]})]});}
            var sketch = newSketch(context, id + "F32", { "sketchPlane" : qUnion([Q0])});
            skCircle(sketch, "E41", {"center": v(-0.4, 40.83) * mm, "radius": 8.06 * mm});
            skSolve(sketch);
        }
        {
            var Q0;
            {var subQ4=sQuery(id+"F2.wireOp",EDGE,"E6.0.4");var subQ8=sQuery(id+"F2.wireOp",EDGE,"E6.0.0");var subQ10=makeQuery(id+"F1.opExtrude","SWEPT_FACE",FACE,{"disambiguationData":[OSD([sQuery(id+"F0.wireOp",EDGE,"E1.right")])]});var subQ11=makeQuery(id+"F5.opExtrude","SWEPT_FACE",FACE,{"disambiguationData":[OSD([sQuery(id+"F4.wireOp",EDGE,"E8.0.0")])]});var subQ15=makeQuery(id+"F1.opExtrude","SWEPT_FACE",FACE,{"disambiguationData":[OSD([sQuery(id+"F0.wireOp",EDGE,"E4.trimOffspring")])]});var subQ18=makeQuery(id+"F3.opExtrude","SWEPT_FACE",FACE,{"disambiguationData":[OSD([subQ8])]});var subQ22=makeQuery(id+"F16.opExtrude","SWEPT_FACE",FACE,{"disambiguationData":[OSD([sQuery(id+"F15.wireOp",EDGE,"E24.right")])]});var subQ24=sQuery(id+"F19.wireOp",EDGE,"E28.bottom");var subQ25=makeQuery(id+"F20.opExtrude","SWEPT_FACE",FACE,{"disambiguationData":[OSD([subQ24])]});var subQ27=makeQuery(id+"F5.opExtrude","SWEPT_FACE",FACE,{"disambiguationData":[OSD([sQuery(id+"F4.wireOp",EDGE,"E8.0.8")])]});var subQ28=makeQuery(id+"F3.opExtrude","SWEPT_FACE",FACE,{"disambiguationData":[OSD([subQ4])]});var subQ29=makeQuery(id+"F1.opExtrude","SWEPT_FACE",FACE,{"disambiguationData":[OSD([sQuery(id+"F0.wireOp",EDGE,"E1.bottom")])]});var subQ30=sQuery(id+"F19.wireOp",EDGE,"E28.left");var subQ31=sQuery(id+"F19.wireOp",EDGE,"E28.top");var subQ32=makeQuery(id+"F20.opExtrude","CAP_FACE",FACE,{"disambiguationData":[OSD([subQ24,subQ31,subQ30,sQuery(id+"F19.wireOp",EDGE,"E28.right")])],"isStart":false});var subQ37=makeQuery(id+"F9.opExtrude","SWEPT_FACE",FACE,{"disambiguationData":[OSD([sQuery(id+"F8.wireOp",EDGE,"E15.MirrorCS")])]});var subQ41=makeQuery(id+"F5.boolean.opBoolean","MERGE",FACE,{"derivedFrom":[makeQuery(id+"F3.boolean.opBoolean","MERGE",FACE,{"derivedFrom":[subQ15,subQ18]}),subQ11]});var subQ48=makeQuery(id+"F5.boolean.opBoolean","MERGE",FACE,{"derivedFrom":[makeQuery(id+"F3.boolean.opBoolean","MERGE",FACE,{"derivedFrom":[subQ29,subQ28]}),subQ27]});Q0=makeQuery(id+"F26.boolean.opBoolean","SPLIT",FACE,{"disambiguationData":[TD([subQ25])],"derivedFrom":makeQuery(id+"F24.boolean.opBoolean","SPLIT",FACE,{"disambiguationData":[TD([subQ10])],"derivedFrom":makeQuery(id+"F20.boolean.opBoolean","MERGE",FACE,{"derivedFrom":[makeQuery(id+"F16.boolean.opBoolean","SPLIT",FACE,{"disambiguationData":[TD([subQ22])],"derivedFrom":subQ48}),makeQuery(id+"F16.boolean.opBoolean","SPLIT",FACE,{"disambiguationData":[TD([makeQuery(id+"F9.opExtrude","SWEPT_FACE",FACE,{"disambiguationData":[OSD([sQuery(id+"F8.wireOp",EDGE,"E14.bottom")])]})])],"derivedFrom":subQ48}),makeQuery(id+"F16.boolean.opBoolean","SPLIT",FACE,{"disambiguationData":[TD([subQ22])],"derivedFrom":subQ41}),makeQuery(id+"F16.boolean.opBoolean","SPLIT",FACE,{"disambiguationData":[TD([subQ37])],"derivedFrom":subQ41}),subQ32]})})});}
            var sketch = newSketch(context, id + "F33", { "sketchPlane" : qUnion([Q0])});
            skCircle(sketch, "E42", {"center": v(-11.5, -187) * mm, "radius": 1.5 * mm});
            skCircle(sketch, "E43.MirrorC", {"center": v(11.5, -187) * mm, "radius": 1.5 * mm});
            skCircle(sketch, "E44", {"center": v(11.5, -90) * mm, "radius": 1.5 * mm});
            skCircle(sketch, "E45.MirrorC", {"center": v(-11.5, -90) * mm, "radius": 1.5 * mm});
            skCircle(sketch, "E46", {"center": v(-11.5, 20) * mm, "radius": 1.5 * mm});
            skCircle(sketch, "E47", {"center": v(11.5, 48.5) * mm, "radius": 1.5 * mm});
            skCircle(sketch, "E48", {"center": v(11.5, 41) * mm, "radius": 1.5 * mm});
            skCircle(sketch, "E49.MirrorC", {"center": v(11.5, 20) * mm, "radius": 1.5 * mm});
            skSolve(sketch);
        }
        {
            var Q0;
            Q0 = qSketchRegion(id + "F33", true);
            var Q1;
            {var subQ9=makeQuery(id+"F1.opExtrude","SWEPT_FACE",FACE,{"disambiguationData":[OSD([sQuery(id+"F0.wireOp",EDGE,"E3.left")])]});var subQ13=makeQuery(id+"F3.opExtrude","SWEPT_FACE",FACE,{"disambiguationData":[OSD([sQuery(id+"F2.wireOp",EDGE,"E6.0.2")])]});var subQ14=makeQuery(id+"F16.opExtrude","SWEPT_FACE",FACE,{"disambiguationData":[OSD([sQuery(id+"F15.wireOp",EDGE,"E24.top")])]});var subQ15=makeQuery(id+"F1.opExtrude","SWEPT_FACE",FACE,{"disambiguationData":[OSD([sQuery(id+"F0.wireOp",EDGE,"E2.0")])]});var subQ18=makeQuery(id+"F5.opExtrude","SWEPT_FACE",FACE,{"disambiguationData":[OSD([sQuery(id+"F4.wireOp",EDGE,"E8.0.10")])]});var subQ19=makeQuery(id+"F16.opExtrude","SWEPT_FACE",FACE,{"disambiguationData":[OSD([sQuery(id+"F15.wireOp",EDGE,"E23.top")])]});var subQ25=makeQuery(id+"F16.boolean.opBoolean","MERGE",FACE,{"derivedFrom":[makeQuery(id+"F5.boolean.opBoolean","MERGE",FACE,{"derivedFrom":[makeQuery(id+"F3.boolean.opBoolean","MERGE",FACE,{"derivedFrom":[subQ15,subQ13]}),subQ18]}),subQ19,subQ14]});Q1=makeQuery(id+"F28.boolean.opBoolean","MERGE",FACE,{"derivedFrom":[makeQuery(id+"F26.boolean.opBoolean","MERGE",FACE,{"derivedFrom":[makeQuery(id+"F20.boolean.opBoolean","SPLIT",FACE,{"disambiguationData":[TD([makeQuery(id+"F20.opExtrude","SWEPT_FACE",FACE,{"disambiguationData":[OSD([sQuery(id+"F19.wireOp",EDGE,"E28.right")])]})])],"derivedFrom":subQ25}),makeQuery(id+"F20.boolean.opBoolean","SPLIT",FACE,{"disambiguationData":[TD([makeQuery(id+"F20.opExtrude","SWEPT_FACE",FACE,{"disambiguationData":[OSD([sQuery(id+"F19.wireOp",EDGE,"E28.left")])]})])],"derivedFrom":subQ25}),makeQuery(id+"F24.boolean.opBoolean","MERGE",FACE,{"derivedFrom":[makeQuery(id+"F20.boolean.opBoolean","SPLIT",FACE,{"disambiguationData":[TD([subQ9])],"derivedFrom":subQ25}),makeQuery(id+"F24.opExtrude","CAP_FACE",FACE,{"disambiguationData":[OSD([sQuery(id+"F23.wireOp",EDGE,"E33")])],"isStart":false})]}),makeQuery(id+"F26.opExtrude","CAP_FACE",FACE,{"disambiguationData":[OSD([sQuery(id+"F25.wireOp",EDGE,"E34.bottom"),sQuery(id+"F25.wireOp",EDGE,"E34.top"),sQuery(id+"F25.wireOp",EDGE,"E34.left"),sQuery(id+"F25.wireOp",EDGE,"E34.right")])],"isStart":true})]}),makeQuery(id+"F28.opExtrude","SWEPT_FACE",FACE,{"disambiguationData":[OSD([sQuery(id+"F27.wireOp",EDGE,"E35.top")])]})]});}
            extrude(context, id + "F34", {"entities" : qUnion([Q0]), "operationType" : NewBodyOperationType.REMOVE, "endBound" : BoundingType.UP_TO_SURFACE, "oppositeDirection" : true, "depth" : 25 * mm, "endBoundEntityFace" : qUnion([Q1]), "offsetDistance" : 25 * mm});
        }
        {
            var Q0;
            {var subQ2=sQuery(id+"F0.wireOp",EDGE,"E1.right");var subQ4=sQuery(id+"F4.wireOp",EDGE,"E9");var subQ5=sQuery(id+"F4.wireOp",EDGE,"E8.0.1");Q0=makeQuery(id+"F9.boolean.opBoolean","SPLIT",FACE,{"disambiguationData":[TD([makeQuery(id+"F5.opExtrude","SWEPT_FACE",FACE,{"disambiguationData":[OSD([subQ4])]})])],"derivedFrom":makeQuery(id+"F5.boolean.opBoolean","MERGE",FACE,{"derivedFrom":[makeQuery(id+"F3.boolean.opBoolean","MERGE",FACE,{"derivedFrom":[makeQuery(id+"F1.opExtrude","SWEPT_FACE",FACE,{"disambiguationData":[OSD([subQ2])]}),makeQuery(id+"F3.opExtrude","SWEPT_FACE",FACE,{"disambiguationData":[OSD([sQuery(id+"F2.wireOp",EDGE,"E6.0.11")])]})]}),makeQuery(id+"F5.opExtrude","SWEPT_FACE",FACE,{"disambiguationData":[OSD([subQ5])]})]})});}
            var sketch = newSketch(context, id + "F35", { "sketchPlane" : qUnion([Q0])});
            skLineSegment(sketch, "E50.0", {"start": v(50, 6.5) * mm, "end": v(32, 6.5) * mm});
            skLineSegment(sketch, "E51.0", {"start": v(32, 5.5) * mm, "end": v(32, 6.5) * mm});
            skLineSegment(sketch, "E52.0", {"start": v(50, 5.5) * mm, "end": v(50, 6.5) * mm});
            skLineSegment(sketch, "E53", {"start": v(50, 5.5) * mm, "end": v(32, 5.5) * mm});
            skSolve(sketch);
        }
        {
            var Q0;
            Q0 = qSketchRegion(id + "F35", true);
            var Q1;
            {var subQ1=sQuery(id+"F4.wireOp",EDGE,"E8.0.11");Q1=makeQuery(id+"F16.boolean.opBoolean","SPLIT",FACE,{"disambiguationData":[TD([makeQuery(id+"F16.opExtrude","SWEPT_FACE",FACE,{"disambiguationData":[OSD([sQuery(id+"F15.wireOp",EDGE,"E23.left")])]})])],"derivedFrom":makeQuery(id+"F5.boolean.opBoolean","MERGE",FACE,{"derivedFrom":[makeQuery(id+"F3.boolean.opBoolean","MERGE",FACE,{"derivedFrom":[makeQuery(id+"F1.opExtrude","SWEPT_FACE",FACE,{"disambiguationData":[OSD([sQuery(id+"F0.wireOp",EDGE,"E3.right")])]}),makeQuery(id+"F3.opExtrude","SWEPT_FACE",FACE,{"disambiguationData":[OSD([sQuery(id+"F2.wireOp",EDGE,"E6.0.1")])]})]}),makeQuery(id+"F5.opExtrude","SWEPT_FACE",FACE,{"disambiguationData":[OSD([subQ1])]})]})});}
            extrude(context, id + "F36", {"entities" : qUnion([Q0]), "operationType" : NewBodyOperationType.ADD, "endBound" : BoundingType.UP_TO_SURFACE, "oppositeDirection" : true, "depth" : 25 * mm, "endBoundEntityFace" : qUnion([Q1]), "offsetDistance" : 25 * mm});
        }
        {
            var Q0;
            {var subQ2=sQuery(id+"F0.wireOp",EDGE,"E1.right");var subQ4=sQuery(id+"F4.wireOp",EDGE,"E9");var subQ5=sQuery(id+"F4.wireOp",EDGE,"E8.0.1");Q0=makeQuery(id+"F36.boolean.opBoolean","MERGE",FACE,{"derivedFrom":[makeQuery(id+"F9.boolean.opBoolean","SPLIT",FACE,{"disambiguationData":[TD([makeQuery(id+"F5.opExtrude","SWEPT_FACE",FACE,{"disambiguationData":[OSD([subQ4])]})])],"derivedFrom":makeQuery(id+"F5.boolean.opBoolean","MERGE",FACE,{"derivedFrom":[makeQuery(id+"F3.boolean.opBoolean","MERGE",FACE,{"derivedFrom":[makeQuery(id+"F1.opExtrude","SWEPT_FACE",FACE,{"disambiguationData":[OSD([subQ2])]}),makeQuery(id+"F3.opExtrude","SWEPT_FACE",FACE,{"disambiguationData":[OSD([sQuery(id+"F2.wireOp",EDGE,"E6.0.11")])]})]}),makeQuery(id+"F5.opExtrude","SWEPT_FACE",FACE,{"disambiguationData":[OSD([subQ5])]})]})}),makeQuery(id+"F36.opExtrude","CAP_FACE",FACE,{"disambiguationData":[OSD([sQuery(id+"F35.wireOp",EDGE,"E50.0"),sQuery(id+"F35.wireOp",EDGE,"E51.0"),sQuery(id+"F35.wireOp",EDGE,"E52.0"),sQuery(id+"F35.wireOp",EDGE,"E53")])],"isStart":true})]});}
            var sketch = newSketch(context, id + "F37", { "sketchPlane" : qUnion([Q0])});
            skCircle(sketch, "E54", {"center": v(41, 6.25) * mm, "radius": 0.75 * mm});
            skLineSegment(sketch, "E55", {"start": v(43.25, 2.5) * mm, "end": v(43.25, 5.5) * mm});
            skLineSegment(sketch, "E56", {"start": v(43.25, 5.5) * mm, "end": v(34.1, 5.5) * mm});
            skCircle(sketch, "E57", {"center": v(48.5, 6.25) * mm, "radius": 0.75 * mm});
            skSolve(sketch);
        }
        {
            var Q0;
            Q0 = qSketchRegion(id + "F37", true);
            extrude(context, id + "F38", {"entities" : qUnion([Q0]), "operationType" : NewBodyOperationType.REMOVE, "endBound" : BoundingType.THROUGH_ALL, "oppositeDirection" : true, "depth" : 25 * mm, "offsetDistance" : 25 * mm});
        }
        {
            var Q0;
            {var subQ0=makeQuery(id+"F5.opExtrude","SWEPT_FACE",FACE,{"disambiguationData":[OSD([sQuery(id+"F4.wireOp",EDGE,"E8.0.8")])]});var subQ9=makeQuery(id+"F1.opExtrude","SWEPT_FACE",FACE,{"disambiguationData":[OSD([sQuery(id+"F0.wireOp",EDGE,"E1.bottom")])]});var subQ10=sQuery(id+"F2.wireOp",EDGE,"E6.0.4");var subQ11=makeQuery(id+"F3.opExtrude","SWEPT_FACE",FACE,{"disambiguationData":[OSD([subQ10])]});var subQ12=makeQuery(id+"F1.opExtrude","SWEPT_FACE",FACE,{"disambiguationData":[OSD([sQuery(id+"F0.wireOp",EDGE,"E3.left")])]});var subQ13=makeQuery(id+"F1.opExtrude","SWEPT_FACE",FACE,{"disambiguationData":[OSD([sQuery(id+"F0.wireOp",EDGE,"E1.left")])]});var subQ21=makeQuery(id+"F9.opExtrude","SWEPT_FACE",FACE,{"disambiguationData":[OSD([sQuery(id+"F8.wireOp",EDGE,"E14.bottom")])]});var subQ25=sQuery(id+"F19.wireOp",EDGE,"E28.right");var subQ28=sQuery(id+"F2.wireOp",EDGE,"E6.0.0");var subQ30=makeQuery(id+"F16.opExtrude","SWEPT_FACE",FACE,{"disambiguationData":[OSD([sQuery(id+"F15.wireOp",EDGE,"E24.right")])]});var subQ31=sQuery(id+"F19.wireOp",EDGE,"E28.bottom");var subQ32=sQuery(id+"F19.wireOp",EDGE,"E28.top");var subQ39=makeQuery(id+"F5.boolean.opBoolean","MERGE",FACE,{"derivedFrom":[makeQuery(id+"F3.boolean.opBoolean","MERGE",FACE,{"derivedFrom":[makeQuery(id+"F1.opExtrude","SWEPT_FACE",FACE,{"disambiguationData":[OSD([sQuery(id+"F0.wireOp",EDGE,"E4.trimOffspring")])]}),makeQuery(id+"F3.opExtrude","SWEPT_FACE",FACE,{"disambiguationData":[OSD([subQ28])]})]}),makeQuery(id+"F5.opExtrude","SWEPT_FACE",FACE,{"disambiguationData":[OSD([sQuery(id+"F4.wireOp",EDGE,"E8.0.0")])]})]});var subQ40=makeQuery(id+"F5.boolean.opBoolean","MERGE",FACE,{"derivedFrom":[makeQuery(id+"F3.boolean.opBoolean","MERGE",FACE,{"derivedFrom":[subQ9,subQ11]}),subQ0]});Q0=makeQuery(id+"F26.boolean.opBoolean","SPLIT",FACE,{"disambiguationData":[TD([subQ12])],"derivedFrom":makeQuery(id+"F24.boolean.opBoolean","SPLIT",FACE,{"disambiguationData":[TD([subQ13])],"derivedFrom":makeQuery(id+"F20.boolean.opBoolean","MERGE",FACE,{"derivedFrom":[makeQuery(id+"F16.boolean.opBoolean","SPLIT",FACE,{"disambiguationData":[TD([subQ30])],"derivedFrom":subQ40}),makeQuery(id+"F16.boolean.opBoolean","SPLIT",FACE,{"disambiguationData":[TD([subQ21])],"derivedFrom":subQ40}),makeQuery(id+"F16.boolean.opBoolean","SPLIT",FACE,{"disambiguationData":[TD([subQ30])],"derivedFrom":subQ39}),makeQuery(id+"F16.boolean.opBoolean","SPLIT",FACE,{"disambiguationData":[TD([makeQuery(id+"F9.opExtrude","SWEPT_FACE",FACE,{"disambiguationData":[OSD([sQuery(id+"F8.wireOp",EDGE,"E15.MirrorCS")])]})])],"derivedFrom":subQ39}),makeQuery(id+"F20.opExtrude","CAP_FACE",FACE,{"disambiguationData":[OSD([subQ31,subQ32,sQuery(id+"F19.wireOp",EDGE,"E28.left"),subQ25])],"isStart":false})]})})});}
            var sketch = newSketch(context, id + "F39", { "sketchPlane" : qUnion([Q0])});
            skCircle(sketch, "E58.0", {"center": v(-11.5, -187) * mm, "radius": 1.5 * mm});
            skCircle(sketch, "E59.0", {"center": v(11.5, -187) * mm, "radius": 1.5 * mm});
            skCircle(sketch, "E60.0", {"center": v(-11.5, -90) * mm, "radius": 1.5 * mm});
            skCircle(sketch, "E61.0", {"center": v(11.5, -90) * mm, "radius": 1.5 * mm});
            skCircle(sketch, "E62.0", {"center": v(-11.5, 20) * mm, "radius": 1.5 * mm});
            skCircle(sketch, "E63.0", {"center": v(11.5, 20) * mm, "radius": 1.5 * mm});
            skSolve(sketch);
        }
        {
            var Q0;
            Q0 = qSketchRegion(id + "F39", true);
            extrude(context, id + "F40", {"entities" : qUnion([Q0]), "operationType" : NewBodyOperationType.REMOVE, "oppositeDirection" : true, "depth" : 5 * mm, "offsetDistance" : 25 * mm});
        }
        {
            var Q0;
            {var subQ2=makeQuery(id+"F3.opExtrude","SWEPT_FACE",FACE,{"disambiguationData":[OSD([sQuery(id+"F2.wireOp",EDGE,"E6.0.5")])]});var subQ13=sQuery(id+"F0.wireOp",EDGE,"E1.left");var subQ14=makeQuery(id+"F1.opExtrude","SWEPT_FACE",FACE,{"disambiguationData":[OSD([subQ13])]});var subQ15=sQuery(id+"F4.wireOp",EDGE,"E8.0.7");var subQ16=makeQuery(id+"F5.opExtrude","SWEPT_FACE",FACE,{"disambiguationData":[OSD([subQ15])]});var subQ24=sQuery(id+"F4.wireOp",EDGE,"E9");var subQ25=makeQuery(id+"F5.opExtrude","SWEPT_FACE",FACE,{"disambiguationData":[OSD([subQ24])]});var subQ28=sQuery(id+"F0.wireOp",EDGE,"E0.bottom");var subQ30=makeQuery(id+"F1.opExtrude","SWEPT_FACE",FACE,{"disambiguationData":[OSD([subQ28])]});Q0=makeQuery(id+"F30.boolean.opBoolean","SPLIT",FACE,{"disambiguationData":[TD([subQ30])],"derivedFrom":makeQuery(id+"F9.boolean.opBoolean","SPLIT",FACE,{"disambiguationData":[TD([subQ25])],"derivedFrom":makeQuery(id+"F5.boolean.opBoolean","MERGE",FACE,{"derivedFrom":[makeQuery(id+"F3.boolean.opBoolean","MERGE",FACE,{"derivedFrom":[subQ14,subQ2]}),subQ16]})})});}
            var sketch = newSketch(context, id + "F41", { "sketchPlane" : qUnion([Q0])});
            skCircle(sketch, "E64", {"center": v(-25, 6) * mm, "radius": 1.5 * mm});
            skPoint(sketch, "E65", {"position": v(-28.5, 6) * mm});
            skSolve(sketch);
        }
        {
            var Q0;
            Q0 = qSketchRegion(id + "F41", true);
            extrude(context, id + "F42", {"entities" : qUnion([Q0]), "operationType" : NewBodyOperationType.REMOVE, "oppositeDirection" : true, "depth" : 5 * mm, "offsetDistance" : 25 * mm});
        }
        {
            var Q0;
            {var subQ4=sQuery(id+"F2.wireOp",EDGE,"E6.0.4");var subQ8=sQuery(id+"F2.wireOp",EDGE,"E6.0.0");var subQ10=makeQuery(id+"F1.opExtrude","SWEPT_FACE",FACE,{"disambiguationData":[OSD([sQuery(id+"F0.wireOp",EDGE,"E1.right")])]});var subQ11=makeQuery(id+"F5.opExtrude","SWEPT_FACE",FACE,{"disambiguationData":[OSD([sQuery(id+"F4.wireOp",EDGE,"E8.0.0")])]});var subQ15=makeQuery(id+"F1.opExtrude","SWEPT_FACE",FACE,{"disambiguationData":[OSD([sQuery(id+"F0.wireOp",EDGE,"E4.trimOffspring")])]});var subQ18=makeQuery(id+"F3.opExtrude","SWEPT_FACE",FACE,{"disambiguationData":[OSD([subQ8])]});var subQ22=makeQuery(id+"F16.opExtrude","SWEPT_FACE",FACE,{"disambiguationData":[OSD([sQuery(id+"F15.wireOp",EDGE,"E24.right")])]});var subQ24=sQuery(id+"F19.wireOp",EDGE,"E28.bottom");var subQ25=makeQuery(id+"F20.opExtrude","SWEPT_FACE",FACE,{"disambiguationData":[OSD([subQ24])]});var subQ27=makeQuery(id+"F5.opExtrude","SWEPT_FACE",FACE,{"disambiguationData":[OSD([sQuery(id+"F4.wireOp",EDGE,"E8.0.8")])]});var subQ28=makeQuery(id+"F3.opExtrude","SWEPT_FACE",FACE,{"disambiguationData":[OSD([subQ4])]});var subQ29=makeQuery(id+"F1.opExtrude","SWEPT_FACE",FACE,{"disambiguationData":[OSD([sQuery(id+"F0.wireOp",EDGE,"E1.bottom")])]});var subQ30=sQuery(id+"F19.wireOp",EDGE,"E28.left");var subQ31=sQuery(id+"F19.wireOp",EDGE,"E28.top");var subQ32=makeQuery(id+"F20.opExtrude","CAP_FACE",FACE,{"disambiguationData":[OSD([subQ24,subQ31,subQ30,sQuery(id+"F19.wireOp",EDGE,"E28.right")])],"isStart":false});var subQ37=makeQuery(id+"F9.opExtrude","SWEPT_FACE",FACE,{"disambiguationData":[OSD([sQuery(id+"F8.wireOp",EDGE,"E15.MirrorCS")])]});var subQ41=makeQuery(id+"F5.boolean.opBoolean","MERGE",FACE,{"derivedFrom":[makeQuery(id+"F3.boolean.opBoolean","MERGE",FACE,{"derivedFrom":[subQ15,subQ18]}),subQ11]});var subQ48=makeQuery(id+"F5.boolean.opBoolean","MERGE",FACE,{"derivedFrom":[makeQuery(id+"F3.boolean.opBoolean","MERGE",FACE,{"derivedFrom":[subQ29,subQ28]}),subQ27]});Q0=makeQuery(id+"F26.boolean.opBoolean","SPLIT",FACE,{"disambiguationData":[TD([subQ25])],"derivedFrom":makeQuery(id+"F24.boolean.opBoolean","SPLIT",FACE,{"disambiguationData":[TD([subQ10])],"derivedFrom":makeQuery(id+"F20.boolean.opBoolean","MERGE",FACE,{"derivedFrom":[makeQuery(id+"F16.boolean.opBoolean","SPLIT",FACE,{"disambiguationData":[TD([subQ22])],"derivedFrom":subQ48}),makeQuery(id+"F16.boolean.opBoolean","SPLIT",FACE,{"disambiguationData":[TD([makeQuery(id+"F9.opExtrude","SWEPT_FACE",FACE,{"disambiguationData":[OSD([sQuery(id+"F8.wireOp",EDGE,"E14.bottom")])]})])],"derivedFrom":subQ48}),makeQuery(id+"F16.boolean.opBoolean","SPLIT",FACE,{"disambiguationData":[TD([subQ22])],"derivedFrom":subQ41}),makeQuery(id+"F16.boolean.opBoolean","SPLIT",FACE,{"disambiguationData":[TD([subQ37])],"derivedFrom":subQ41}),subQ32]})})});}
            var sketch = newSketch(context, id + "F43", { "sketchPlane" : qUnion([Q0])});
            skLineSegment(sketch, "E66.bottom", {"start": v(7.5, -190) * mm, "end": v(-7.5, -190) * mm});
            skLineSegment(sketch, "E66.top", {"start": v(7.5, -175.93) * mm, "end": v(-7.5, -175.93) * mm});
            skLineSegment(sketch, "E66.left", {"start": v(7.5, -190) * mm, "end": v(7.5, -175.93) * mm});
            skLineSegment(sketch, "E66.right", {"start": v(-7.5, -190) * mm, "end": v(-7.5, -175.93) * mm});
            skSolve(sketch);
        }
        {
            var Q0;
            Q0 = qSketchRegion(id + "F43", true);
            var Q1;
            {var subQ9=makeQuery(id+"F1.opExtrude","SWEPT_FACE",FACE,{"disambiguationData":[OSD([sQuery(id+"F0.wireOp",EDGE,"E3.left")])]});var subQ13=makeQuery(id+"F3.opExtrude","SWEPT_FACE",FACE,{"disambiguationData":[OSD([sQuery(id+"F2.wireOp",EDGE,"E6.0.2")])]});var subQ14=makeQuery(id+"F16.opExtrude","SWEPT_FACE",FACE,{"disambiguationData":[OSD([sQuery(id+"F15.wireOp",EDGE,"E24.top")])]});var subQ15=makeQuery(id+"F1.opExtrude","SWEPT_FACE",FACE,{"disambiguationData":[OSD([sQuery(id+"F0.wireOp",EDGE,"E2.0")])]});var subQ18=makeQuery(id+"F5.opExtrude","SWEPT_FACE",FACE,{"disambiguationData":[OSD([sQuery(id+"F4.wireOp",EDGE,"E8.0.10")])]});var subQ19=makeQuery(id+"F16.opExtrude","SWEPT_FACE",FACE,{"disambiguationData":[OSD([sQuery(id+"F15.wireOp",EDGE,"E23.top")])]});var subQ25=makeQuery(id+"F16.boolean.opBoolean","MERGE",FACE,{"derivedFrom":[makeQuery(id+"F5.boolean.opBoolean","MERGE",FACE,{"derivedFrom":[makeQuery(id+"F3.boolean.opBoolean","MERGE",FACE,{"derivedFrom":[subQ15,subQ13]}),subQ18]}),subQ19,subQ14]});Q1=makeQuery(id+"F28.boolean.opBoolean","MERGE",FACE,{"derivedFrom":[makeQuery(id+"F26.boolean.opBoolean","MERGE",FACE,{"derivedFrom":[makeQuery(id+"F20.boolean.opBoolean","SPLIT",FACE,{"disambiguationData":[TD([makeQuery(id+"F20.opExtrude","SWEPT_FACE",FACE,{"disambiguationData":[OSD([sQuery(id+"F19.wireOp",EDGE,"E28.right")])]})])],"derivedFrom":subQ25}),makeQuery(id+"F20.boolean.opBoolean","SPLIT",FACE,{"disambiguationData":[TD([makeQuery(id+"F20.opExtrude","SWEPT_FACE",FACE,{"disambiguationData":[OSD([sQuery(id+"F19.wireOp",EDGE,"E28.left")])]})])],"derivedFrom":subQ25}),makeQuery(id+"F24.boolean.opBoolean","MERGE",FACE,{"derivedFrom":[makeQuery(id+"F20.boolean.opBoolean","SPLIT",FACE,{"disambiguationData":[TD([subQ9])],"derivedFrom":subQ25}),makeQuery(id+"F24.opExtrude","CAP_FACE",FACE,{"disambiguationData":[OSD([sQuery(id+"F23.wireOp",EDGE,"E33")])],"isStart":false})]}),makeQuery(id+"F26.opExtrude","CAP_FACE",FACE,{"disambiguationData":[OSD([sQuery(id+"F25.wireOp",EDGE,"E34.bottom"),sQuery(id+"F25.wireOp",EDGE,"E34.top"),sQuery(id+"F25.wireOp",EDGE,"E34.left"),sQuery(id+"F25.wireOp",EDGE,"E34.right")])],"isStart":true})]}),makeQuery(id+"F28.opExtrude","SWEPT_FACE",FACE,{"disambiguationData":[OSD([sQuery(id+"F27.wireOp",EDGE,"E35.top")])]})]});}
            extrude(context, id + "F44", {"entities" : qUnion([Q0]), "operationType" : NewBodyOperationType.REMOVE, "endBound" : BoundingType.UP_TO_SURFACE, "oppositeDirection" : true, "depth" : 25 * mm, "endBoundEntityFace" : qUnion([Q1]), "offsetDistance" : 25 * mm});
        }
        {
            var Q0;
            {var subQ2=sQuery(id+"F4.wireOp",EDGE,"E8.0.0");Q0=makeQuery(id+"F16.boolean.opBoolean","SPLIT",FACE,{"disambiguationData":[TD([makeQuery(id+"F16.opExtrude","SWEPT_FACE",FACE,{"disambiguationData":[OSD([sQuery(id+"F15.wireOp",EDGE,"E23.left")])]})])],"derivedFrom":makeQuery(id+"F5.boolean.opBoolean","MERGE",FACE,{"derivedFrom":[makeQuery(id+"F3.boolean.opBoolean","MERGE",FACE,{"derivedFrom":[makeQuery(id+"F1.opExtrude","SWEPT_FACE",FACE,{"disambiguationData":[OSD([sQuery(id+"F0.wireOp",EDGE,"E4.trimOffspring")])]}),makeQuery(id+"F3.opExtrude","SWEPT_FACE",FACE,{"disambiguationData":[OSD([sQuery(id+"F2.wireOp",EDGE,"E6.0.0")])]})]}),makeQuery(id+"F5.opExtrude","SWEPT_FACE",FACE,{"disambiguationData":[OSD([subQ2])]})]})});}
            var sketch = newSketch(context, id + "F45", { "sketchPlane" : qUnion([Q0])});
            skCircle(sketch, "E67.0", {"center": v(11.5, 41) * mm, "radius": 1.5 * mm});
            skCircle(sketch, "E68.0", {"center": v(11.5, 48.5) * mm, "radius": 1.5 * mm});
            skSolve(sketch);
        }
        {
            var Q0;
            Q0 = qSketchRegion(id + "F45", true);
            extrude(context, id + "F46", {"entities" : qUnion([Q0]), "operationType" : NewBodyOperationType.REMOVE, "oppositeDirection" : true, "depth" : 4 * mm, "offsetDistance" : 25 * mm});
        }
    });
